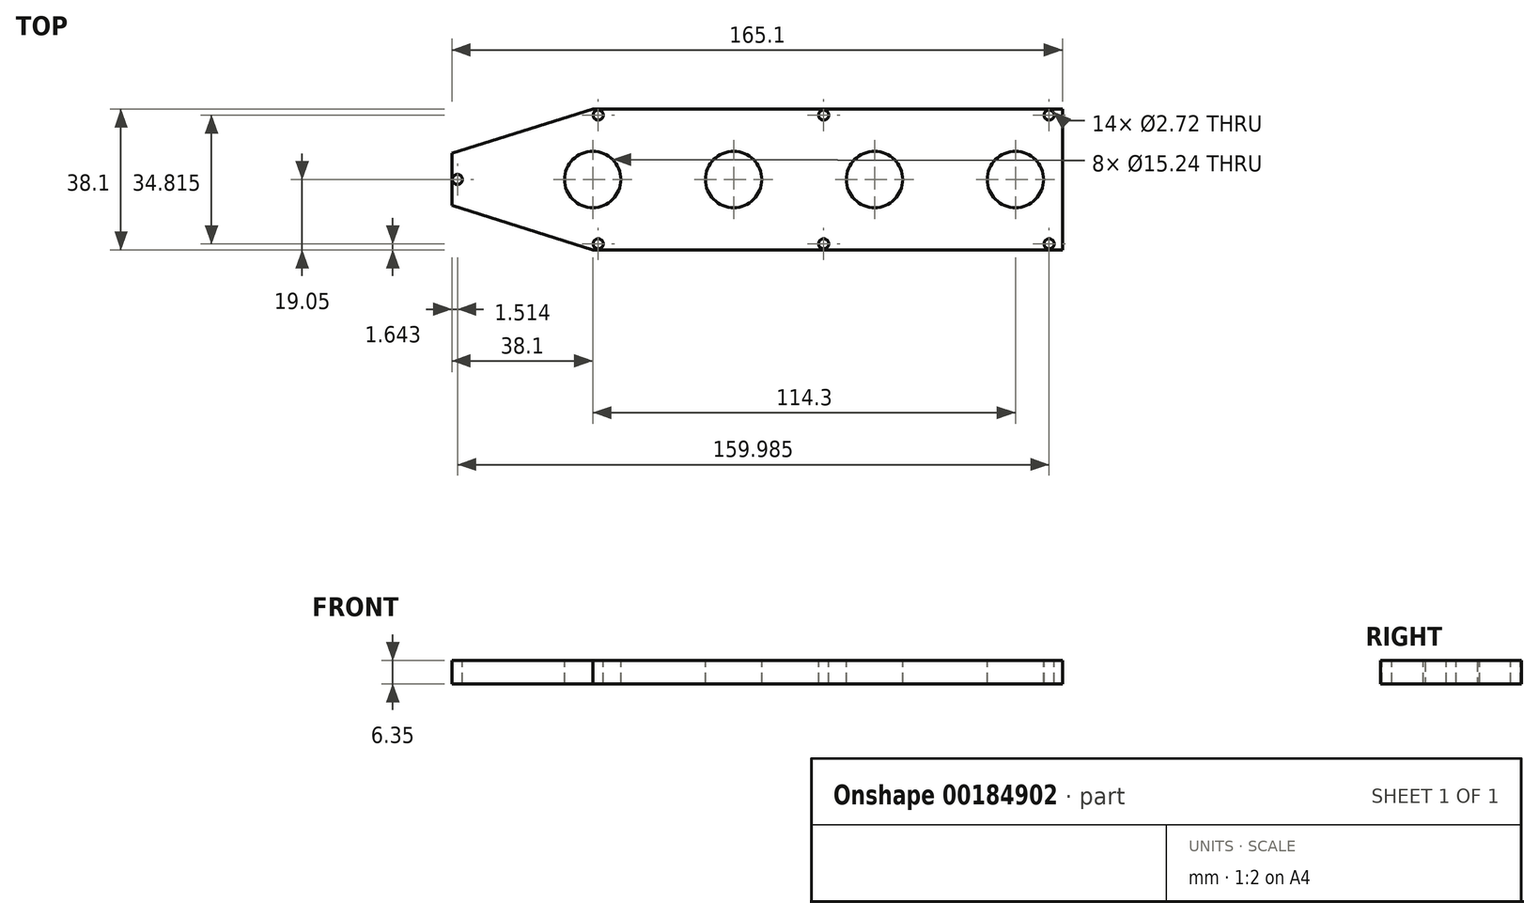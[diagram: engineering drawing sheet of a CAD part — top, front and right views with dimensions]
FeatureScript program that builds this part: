
annotation { "Feature Type Name" : "Feature", "Feature Type Description" : "" }
export const myFeature = defineFeature(function(context is Context, id is Id, definition is map)
    precondition{}
    {
        {
            var Q0;
            Q0=qCreatedBy(makeId("Top.planeOp"),FACE);
            var sketch = newSketch(context, id + "F0", { "sketchPlane" : qUnion([Q0])});
            skLineSegment(sketch, "E0", {"start": v(0, 19.05) * mm, "end": v(-38.1, 7.04) * mm});
            skLineSegment(sketch, "E1", {"start": v(-38.1, 7.04) * mm, "end": v(-38.1, -7.04) * mm});
            skLineSegment(sketch, "E2", {"start": v(-38.1, -7.04) * mm, "end": v(0, -19.05) * mm});
            skLineSegment(sketch, "E3", {"start": v(0, 19.05) * mm, "end": v(127, 19.05) * mm});
            skLineSegment(sketch, "E4", {"start": v(0, -19.05) * mm, "end": v(127, -19.05) * mm});
            skLineSegment(sketch, "E5", {"start": v(127, -19.05) * mm, "end": v(127, 19.05) * mm});
            skPoint(sketch, "E6", {"position": v(-38.1, 0) * mm});
            skSolve(sketch);
        }
        {
            var Q0;
            Q0=makeQuery(id+"F0.imprint","IMPRINT",FACE,{"disambiguationData":[TD([[makeQuery(id+"F0.imprint","IMPRINT",EDGE,{"derivedFrom":sQuery(id+"F0.wireOp",EDGE,"E0")}),1.0]])]});
            extrude(context, id + "F1", {"entities" : qUnion([Q0]), "depth" : 6.35 * mm});
        }
        {
            var Q0;
            Q0=makeQuery(id+"F1.opExtrude","CAP_FACE",FACE,{"disambiguationData":[OSD([sQuery(id+"F0.wireOp",EDGE,"E0"),sQuery(id+"F0.wireOp",EDGE,"E1"),sQuery(id+"F0.wireOp",EDGE,"E2"),sQuery(id+"F0.wireOp",EDGE,"E3"),sQuery(id+"F0.wireOp",EDGE,"E4"),sQuery(id+"F0.wireOp",EDGE,"E5")])],"isStart":false});
            var sketch = newSketch(context, id + "F2", { "sketchPlane" : qUnion([Q0])});
            skCircle(sketch, "E7", {"center": v(1.48, 17.4) * mm, "radius": 1.36 * mm});
            skCircle(sketch, "E8.1.0.0", {"center": v(62.44, 17.4) * mm, "radius": 1.36 * mm});
            skCircle(sketch, "E8.2.0.0", {"center": v(123.4, 17.4) * mm, "radius": 1.36 * mm});
            skLineSegment(sketch, "E8.direction1", {"start": v(1.48, 17.4) * mm, "end": v(62.44, 17.4) * mm, "construction": true});
            skCircle(sketch, "E9", {"center": v(-36.59, 0) * mm, "radius": 1.36 * mm});
            skCircle(sketch, "E10", {"center": v(1.48, -17.4) * mm, "radius": 1.36 * mm});
            skCircle(sketch, "E11.1.0.0", {"center": v(62.44, -17.4) * mm, "radius": 1.36 * mm});
            skCircle(sketch, "E11.2.0.0", {"center": v(123.4, -17.4) * mm, "radius": 1.36 * mm});
            skLineSegment(sketch, "E11.direction1", {"start": v(1.48, -17.4) * mm, "end": v(62.44, -17.4) * mm, "construction": true});
            skCircle(sketch, "E12", {"center": v(0, 0) * mm, "radius": 7.62 * mm});
            skCircle(sketch, "E13.1.0.0", {"center": v(38.1, 0) * mm, "radius": 7.62 * mm});
            skCircle(sketch, "E13.2.0.0", {"center": v(76.2, 0) * mm, "radius": 7.62 * mm});
            skLineSegment(sketch, "E13.direction1", {"start": v(0, 0) * mm, "end": v(38.1, 0) * mm, "construction": true});
            skCircle(sketch, "E14.0.3.0", {"center": v(114.3, 0) * mm, "radius": 7.62 * mm});
            skSolve(sketch);
        }
        {
            var Q0;
            Q0=makeQuery(id+"F2.imprint","IMPRINT",FACE,{"disambiguationData":[TD([[makeQuery(id+"F2.imprint","IMPRINT",EDGE,{"derivedFrom":sQuery(id+"F2.wireOp",EDGE,"E7")}),1.0]])]});
            var Q1;
            Q1=makeQuery(id+"F2.imprint","IMPRINT",FACE,{"disambiguationData":[TD([[makeQuery(id+"F2.imprint","IMPRINT",EDGE,{"derivedFrom":sQuery(id+"F2.wireOp",EDGE,"E8.1.0.0")}),1.0]])]});
            var Q2;
            Q2=makeQuery(id+"F2.imprint","IMPRINT",FACE,{"disambiguationData":[TD([[makeQuery(id+"F2.imprint","IMPRINT",EDGE,{"derivedFrom":sQuery(id+"F2.wireOp",EDGE,"E8.2.0.0")}),1.0]])]});
            var Q3;
            Q3=makeQuery(id+"F2.imprint","IMPRINT",FACE,{"disambiguationData":[TD([[makeQuery(id+"F2.imprint","IMPRINT",EDGE,{"derivedFrom":sQuery(id+"F2.wireOp",EDGE,"E11.2.0.0")}),1.0]])]});
            var Q4;
            Q4=makeQuery(id+"F2.imprint","IMPRINT",FACE,{"disambiguationData":[TD([[makeQuery(id+"F2.imprint","IMPRINT",EDGE,{"derivedFrom":sQuery(id+"F2.wireOp",EDGE,"E11.1.0.0")}),1.0]])]});
            var Q5;
            Q5=makeQuery(id+"F2.imprint","IMPRINT",FACE,{"disambiguationData":[TD([[makeQuery(id+"F2.imprint","IMPRINT",EDGE,{"derivedFrom":sQuery(id+"F2.wireOp",EDGE,"E10")}),1.0]])]});
            var Q6;
            Q6=makeQuery(id+"F2.imprint","IMPRINT",FACE,{"disambiguationData":[TD([[makeQuery(id+"F2.imprint","IMPRINT",EDGE,{"derivedFrom":sQuery(id+"F2.wireOp",EDGE,"E9")}),1.0]])]});
            var Q7;
            Q7=makeQuery(id+"F2.imprint","IMPRINT",FACE,{"disambiguationData":[TD([[makeQuery(id+"F2.imprint","IMPRINT",EDGE,{"derivedFrom":sQuery(id+"F2.wireOp",EDGE,"E12")}),1.0]])]});
            var Q8;
            Q8=makeQuery(id+"F2.imprint","IMPRINT",FACE,{"disambiguationData":[TD([[makeQuery(id+"F2.imprint","IMPRINT",EDGE,{"derivedFrom":sQuery(id+"F2.wireOp",EDGE,"E13.1.0.0")}),1.0]])]});
            var Q9;
            Q9=makeQuery(id+"F2.imprint","IMPRINT",FACE,{"disambiguationData":[TD([[makeQuery(id+"F2.imprint","IMPRINT",EDGE,{"derivedFrom":sQuery(id+"F2.wireOp",EDGE,"E13.2.0.0")}),1.0]])]});
            var Q10;
            Q10=makeQuery(id+"F2.imprint","IMPRINT",FACE,{"disambiguationData":[TD([[makeQuery(id+"F2.imprint","IMPRINT",EDGE,{"derivedFrom":sQuery(id+"F2.wireOp",EDGE,"E14.0.3.0")}),1.0]])]});
            extrude(context, id + "F3", {"entities" : qUnion([Q0, Q1, Q2, Q3, Q4, Q5, Q6, Q7, Q8, Q9, Q10]), "operationType" : NewBodyOperationType.REMOVE, "oppositeDirection" : true, "depth" : 25.4 * mm});
        }
    });
